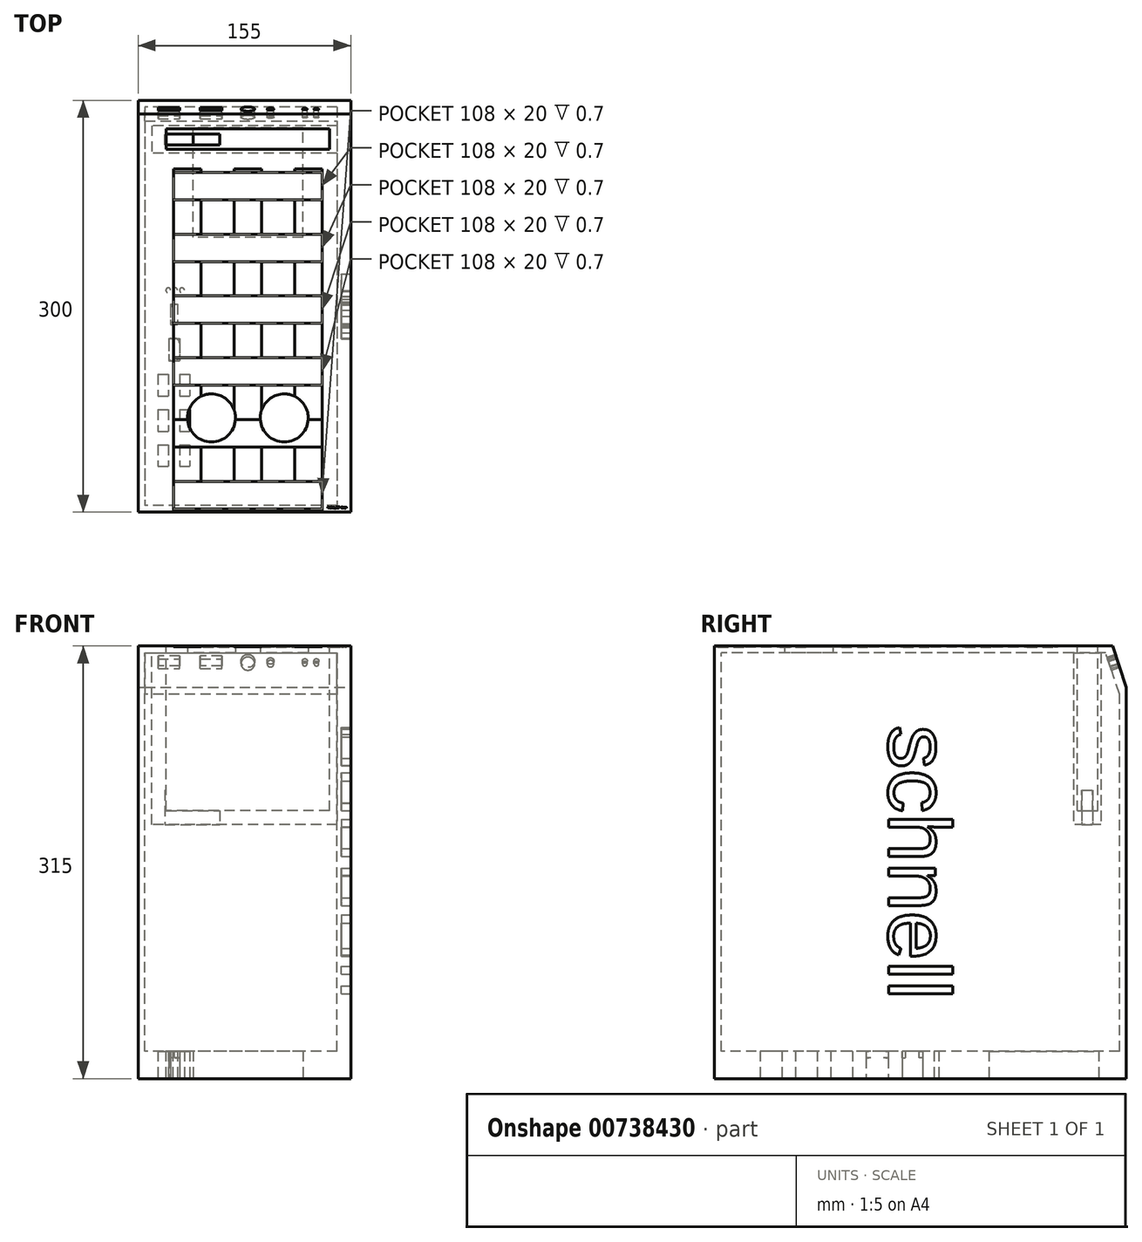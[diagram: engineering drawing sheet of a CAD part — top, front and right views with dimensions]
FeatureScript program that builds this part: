
annotation { "Feature Type Name" : "Feature", "Feature Type Description" : "" }
export const myFeature = defineFeature(function(context is Context, id is Id, definition is map)
    precondition{}
    {
        {
            var Q0;
            Q0=qCreatedBy(makeId("Top.planeOp"),FACE);
            var sketch = newSketch(context, id + "F0", { "sketchPlane" : qUnion([Q0])});
            skLineSegment(sketch, "E0.bottom", {"start": v(75, -150) * mm, "end": v(-75, -150) * mm});
            skLineSegment(sketch, "E0.top", {"start": v(75, 150) * mm, "end": v(-75, 150) * mm});
            skLineSegment(sketch, "E0.left", {"start": v(75, -150) * mm, "end": v(75, 150) * mm});
            skLineSegment(sketch, "E0.right", {"start": v(-75, -150) * mm, "end": v(-75, 150) * mm});
            skPoint(sketch, "E0.middle", {"position": v(0, 0) * mm});
            skSolve(sketch);
        }
        {
            var Q0;
            Q0 = qSketchRegion(id + "F0", true);
            extrude(context, id + "F1", {"entities" : qUnion([Q0]), "depth" : 300 * mm, "offsetDistance" : 25 * mm});
        }
        {
            var Q0;
            Q0=makeQuery(id+"F1.opExtrude","SWEPT_FACE",FACE,{"disambiguationData":[OSD([sQuery(id+"F0.wireOp",EDGE,"E0.left")])]});
            var sketch = newSketch(context, id + "F2", { "sketchPlane" : qUnion([Q0])});
            skLineSegment(sketch, "E1.bottom", {"start": v(145, 295) * mm, "end": v(-145, 295) * mm});
            skLineSegment(sketch, "E1.top", {"start": v(145, 5) * mm, "end": v(-145, 5) * mm});
            skLineSegment(sketch, "E1.left", {"start": v(145, 295) * mm, "end": v(145, 5) * mm});
            skLineSegment(sketch, "E1.right", {"start": v(-145, 295) * mm, "end": v(-145, 5) * mm});
            skPoint(sketch, "E1.middle", {"position": v(0, 150) * mm});
            skPoint(sketch, "E1.middle.positionSnap0", {"position": v(-150, 150) * mm});
            skPoint(sketch, "E1.centerSnap0", {"position": v(-150, 150) * mm});
            skSolve(sketch);
        }
        {
            var Q0;
            Q0 = qSketchRegion(id + "F2", true);
            extrude(context, id + "F3", {"entities" : qUnion([Q0]), "operationType" : NewBodyOperationType.REMOVE, "oppositeDirection" : true, "depth" : 140 * mm, "offsetDistance" : 25 * mm});
        }
        {
            var Q0;
            Q0=qCreatedBy(makeId("Top.planeOp"),FACE);
            var sketch = newSketch(context, id + "F4", { "sketchPlane" : qUnion([Q0])});
            skLineSegment(sketch, "E2.bottom", {"start": v(-70, 131.53) * mm, "end": v(70, 131.53) * mm});
            skLineSegment(sketch, "E2.top", {"start": v(-70, 111.53) * mm, "end": v(70, 111.53) * mm});
            skLineSegment(sketch, "E2.left", {"start": v(-70, 131.53) * mm, "end": v(-70, 111.53) * mm});
            skLineSegment(sketch, "E2.right", {"start": v(70, 131.53) * mm, "end": v(70, 111.53) * mm});
            skPoint(sketch, "E2.middle", {"position": v(0, 121.53) * mm});
            skSolve(sketch);
        }
        {
            var Q0;
            Q0 = qSketchRegion(id + "F4", true);
            extrude(context, id + "F5", {"entities" : qUnion([Q0]), "operationType" : NewBodyOperationType.ADD, "depth" : 130 * mm, "offsetDistance" : 25 * mm});
        }
        {
            var Q0;
            Q0=makeQuery(id+"F4.imprint","IMPRINT",FACE,{"disambiguationData":[TD([[makeQuery(id+"F4.imprint","IMPRINT",EDGE,{"derivedFrom":sQuery(id+"F4.wireOp",EDGE,"E2.bottom")}),-1.0]])]});
            var sketch = newSketch(context, id + "F6", { "sketchPlane" : qUnion([Q0])});
            skLineSegment(sketch, "E3.bottom", {"start": v(-59.38, 114.4) * mm, "end": v(59.38, 114.4) * mm});
            skLineSegment(sketch, "E3.top", {"start": v(-59.38, 129.2) * mm, "end": v(59.38, 129.2) * mm});
            skLineSegment(sketch, "E3.left", {"start": v(-59.38, 114.4) * mm, "end": v(-59.38, 129.2) * mm});
            skLineSegment(sketch, "E3.right", {"start": v(59.38, 114.4) * mm, "end": v(59.38, 129.2) * mm});
            skPoint(sketch, "E3.middle", {"position": v(0, 121.8) * mm});
            skSolve(sketch);
        }
        {
            var Q0;
            Q0 = qSketchRegion(id + "F6", true);
            extrude(context, id + "F7", {"entities" : qUnion([Q0]), "operationType" : NewBodyOperationType.REMOVE, "oppositeDirection" : true, "depth" : -120 * mm, "offsetDistance" : 25 * mm});
        }
        {
            var Q0;
            Q0=makeQuery(id+"F1.opExtrude","SWEPT_BODY",BODY,{"disambiguationData":[OSD([sQuery(id+"F0.wireOp",EDGE,"E0.bottom"),sQuery(id+"F0.wireOp",EDGE,"E0.top"),sQuery(id+"F0.wireOp",EDGE,"E0.left"),sQuery(id+"F0.wireOp",EDGE,"E0.right")])]});
            var Q1;
            Q1=sQuery(id+"F2.wireOp",EDGE,"E1.right");
            transform(context, id + "F8", {"entities" : qUnion([Q0]), "transformType" : TransformType.ROTATION, "transformAxis" : qUnion([Q1]), "angle" : 180 * degree, "makeCopy" : false});
        }
        {
            var Q0;
            Q0=makeQuery(id+"F1.opExtrude","SWEPT_BODY",BODY,{"disambiguationData":[OSD([sQuery(id+"F0.wireOp",EDGE,"E0.bottom"),sQuery(id+"F0.wireOp",EDGE,"E0.top"),sQuery(id+"F0.wireOp",EDGE,"E0.left"),sQuery(id+"F0.wireOp",EDGE,"E0.right")])]});
            var Q1;
            Q1=makeQuery(id+"F1.opExtrude","CAP_EDGE",EDGE,{"disambiguationData":[OSD([sQuery(id+"F0.wireOp",EDGE,"E0.bottom")])],"isStart":true});
            transform(context, id + "F9", {"entities" : qUnion([Q0]), "transformType" : TransformType.ROTATION, "transformAxis" : qUnion([Q1]), "angle" : 180 * degree, "makeCopy" : false});
        }
        {
            var Q0;
            Q0=makeQuery(id+"F1.opExtrude","CAP_EDGE",EDGE,{"disambiguationData":[OSD([sQuery(id+"F0.wireOp",EDGE,"E0.top")])],"isStart":true});
            var Q1;
            Q1=makeQuery(id+"F3.boolean.opBoolean","COPY",EDGE,{"derivedFrom":makeQuery(id+"F3.opExtrude","SWEPT_EDGE",EDGE,{"disambiguationData":[OSD([sQuery(id+"F2.wireOp",EDGE,"E1.top"),sQuery(id+"F2.wireOp",EDGE,"E1.left")])]})});
            chamfer(context, id + "F10", {"entities" : qUnion([Q0, Q1]), "chamferType" : ChamferType.TWO_OFFSETS, "width1" : 30 * mm, "oppositeDirection" : false, "width2" : 10 * mm, "tangentPropagation" : true});
        }
        {
            var Q0;
            Q0=makeQuery(id+"F10.opChamfer","BLEND_FACE",FACE,{"disambiguationData":[OSD([sQuery(id+"F0.wireOp",EDGE,"E0.top")])]});
            var sketch = newSketch(context, id + "F11", { "sketchPlane" : qUnion([Q0])});
            skLineSegment(sketch, "E4.bottom", {"start": v(-100.37, -55.09) * mm, "end": v(-84.67, -55.09) * mm});
            skLineSegment(sketch, "E4.top", {"start": v(-100.37, -62.59) * mm, "end": v(-84.67, -62.59) * mm});
            skLineSegment(sketch, "E4.left", {"start": v(-100.37, -55.09) * mm, "end": v(-100.37, -62.59) * mm});
            skLineSegment(sketch, "E4.right", {"start": v(-84.67, -55.09) * mm, "end": v(-84.67, -62.59) * mm});
            skPoint(sketch, "E4.middle", {"position": v(-92.52, -58.84) * mm});
            skLineSegment(sketch, "E5.bottom", {"start": v(-131.07, -55.09) * mm, "end": v(-115.37, -55.09) * mm});
            skLineSegment(sketch, "E5.top", {"start": v(-131.07, -62.59) * mm, "end": v(-115.37, -62.59) * mm});
            skLineSegment(sketch, "E5.left", {"start": v(-131.07, -55.09) * mm, "end": v(-131.07, -62.59) * mm});
            skLineSegment(sketch, "E5.right", {"start": v(-115.37, -55.09) * mm, "end": v(-115.37, -62.59) * mm});
            skPoint(sketch, "E5.middle", {"position": v(-123.22, -58.84) * mm});
            skPoint(sketch, "E5.cornerSnap0", {"position": v(-92.52, -55.09) * mm});
            skCircle(sketch, "E6", {"center": v(-191.47, -58.84) * mm, "radius": 1.75 * mm});
            skCircle(sketch, "E7", {"center": v(-199.97, -58.84) * mm, "radius": 1.75 * mm});
            skCircle(sketch, "E8", {"center": v(-150, -58.84) * mm, "radius": 5 * mm});
            skPoint(sketch, "E8.centerSnap0", {"position": v(-131.07, -58.84) * mm});
            skCircle(sketch, "E9", {"center": v(-166.5, -58.84) * mm, "radius": 2.5 * mm});
            skSolve(sketch);
        }
        {
            var Q0;
            Q0 = qSketchRegion(id + "F11", true);
            extrude(context, id + "F12", {"entities" : qUnion([Q0]), "operationType" : NewBodyOperationType.REMOVE, "oppositeDirection" : true, "depth" : 10 * mm, "offsetDistance" : 25 * mm});
        }
        {
            var Q0;
            Q0=makeQuery(id+"F11.imprint","IMPRINT",FACE,{"disambiguationData":[TD([[makeQuery(id+"F11.imprint","IMPRINT",EDGE,{"derivedFrom":sQuery(id+"F11.wireOp",EDGE,"E5.bottom")}),-1.0]])]});
            extrude(context, id + "F13", {"entities" : qUnion([Q0]), "operationType" : NewBodyOperationType.REMOVE, "oppositeDirection" : true, "depth" : 10 * mm, "offsetDistance" : 25 * mm});
        }
        {
            var Q0;
            Q0=makeQuery(id+"F1.opExtrude","CAP_FACE",FACE,{"disambiguationData":[OSD([sQuery(id+"F0.wireOp",EDGE,"E0.bottom"),sQuery(id+"F0.wireOp",EDGE,"E0.top"),sQuery(id+"F0.wireOp",EDGE,"E0.left"),sQuery(id+"F0.wireOp",EDGE,"E0.right")])],"isStart":false});
            var sketch = newSketch(context, id + "F14", { "sketchPlane" : qUnion([Q0])});
            skLineSegment(sketch, "E10.bottom", {"start": v(100.26, 91) * mm, "end": v(107.76, 91) * mm});
            skLineSegment(sketch, "E10.top", {"start": v(100.26, 106.7) * mm, "end": v(107.76, 106.7) * mm});
            skLineSegment(sketch, "E10.left", {"start": v(100.26, 91) * mm, "end": v(100.26, 106.7) * mm});
            skLineSegment(sketch, "E10.right", {"start": v(107.76, 91) * mm, "end": v(107.76, 106.7) * mm});
            skPoint(sketch, "E10.middle", {"position": v(104, 98.84) * mm});
            skLineSegment(sketch, "E11.bottom", {"start": v(84.56, 91) * mm, "end": v(92.06, 91) * mm});
            skLineSegment(sketch, "E11.top", {"start": v(84.56, 106.7) * mm, "end": v(92.06, 106.7) * mm});
            skLineSegment(sketch, "E11.left", {"start": v(84.56, 91) * mm, "end": v(84.56, 106.7) * mm});
            skLineSegment(sketch, "E11.right", {"start": v(92.06, 91) * mm, "end": v(92.06, 106.7) * mm});
            skPoint(sketch, "E11.middle", {"position": v(88.3, 98.84) * mm});
            skLineSegment(sketch, "E12.bottom", {"start": v(100.26, 65.3) * mm, "end": v(107.76, 65.3) * mm});
            skLineSegment(sketch, "E12.top", {"start": v(100.26, 81) * mm, "end": v(107.76, 81) * mm});
            skLineSegment(sketch, "E12.left", {"start": v(100.26, 65.3) * mm, "end": v(100.26, 81) * mm});
            skLineSegment(sketch, "E12.right", {"start": v(107.76, 65.3) * mm, "end": v(107.76, 81) * mm});
            skPoint(sketch, "E12.middle", {"position": v(104, 73.14) * mm});
            skLineSegment(sketch, "E13.bottom", {"start": v(84.56, 65.3) * mm, "end": v(92.06, 65.3) * mm});
            skLineSegment(sketch, "E13.top", {"start": v(84.56, 81) * mm, "end": v(92.06, 81) * mm});
            skLineSegment(sketch, "E13.left", {"start": v(84.56, 65.3) * mm, "end": v(84.56, 81) * mm});
            skLineSegment(sketch, "E13.right", {"start": v(92.06, 65.3) * mm, "end": v(92.06, 81) * mm});
            skPoint(sketch, "E13.middle", {"position": v(88.3, 73.14) * mm});
            skPoint(sketch, "E13.middle.positionSnap0", {"position": v(88.3, 91) * mm});
            skPoint(sketch, "E13.centerSnap0", {"position": v(88.3, 91) * mm});
            skLineSegment(sketch, "E14.bottom", {"start": v(100.26, 39.6) * mm, "end": v(107.76, 39.6) * mm});
            skLineSegment(sketch, "E14.top", {"start": v(100.26, 55.3) * mm, "end": v(107.76, 55.3) * mm});
            skLineSegment(sketch, "E14.left", {"start": v(100.26, 39.6) * mm, "end": v(100.26, 55.3) * mm});
            skLineSegment(sketch, "E14.right", {"start": v(107.76, 39.6) * mm, "end": v(107.76, 55.3) * mm});
            skPoint(sketch, "E14.middle", {"position": v(104, 47.44) * mm});
            skLineSegment(sketch, "E15.bottom", {"start": v(84.56, 39.6) * mm, "end": v(92.06, 39.6) * mm});
            skLineSegment(sketch, "E15.top", {"start": v(84.56, 55.3) * mm, "end": v(92.06, 55.3) * mm});
            skLineSegment(sketch, "E15.left", {"start": v(84.56, 39.6) * mm, "end": v(84.56, 55.3) * mm});
            skLineSegment(sketch, "E15.right", {"start": v(92.06, 39.6) * mm, "end": v(92.06, 55.3) * mm});
            skPoint(sketch, "E15.middle", {"position": v(88.3, 47.44) * mm});
            skSolve(sketch);
        }
        {
            var Q0;
            Q0 = qSketchRegion(id + "F14", true);
            extrude(context, id + "F15", {"entities" : qUnion([Q0]), "operationType" : NewBodyOperationType.REMOVE, "oppositeDirection" : true, "depth" : 10 * mm, "offsetDistance" : 25 * mm});
        }
        {
            var Q0;
            Q0=makeQuery(id+"F1.opExtrude","CAP_FACE",FACE,{"disambiguationData":[OSD([sQuery(id+"F0.wireOp",EDGE,"E0.bottom"),sQuery(id+"F0.wireOp",EDGE,"E0.top"),sQuery(id+"F0.wireOp",EDGE,"E0.left"),sQuery(id+"F0.wireOp",EDGE,"E0.right")])],"isStart":false});
            extrude(context, id + "F16", {"entities" : qUnion([Q0]), "operationType" : NewBodyOperationType.ADD, "depth" : 25 * mm, "offsetDistance" : 25 * mm});
        }
        {
            var Q0;
            Q0=makeQuery(id+"F16.opExtrude","CAP_FACE",FACE,{"disambiguationData":[OSD([sQuery(id+"F0.wireOp",EDGE,"E0.bottom"),sQuery(id+"F0.wireOp",EDGE,"E0.top"),sQuery(id+"F0.wireOp",EDGE,"E0.left"),sQuery(id+"F0.wireOp",EDGE,"E0.right")])],"isStart":false});
            var sketch = newSketch(context, id + "F17", { "sketchPlane" : qUnion([Q0])});
            skLineSegment(sketch, "E16.bottom", {"start": v(92.28, 13.4) * mm, "end": v(100.18, 13.4) * mm});
            skLineSegment(sketch, "E16.top", {"start": v(92.28, 29.6) * mm, "end": v(100.18, 29.6) * mm});
            skLineSegment(sketch, "E16.left", {"start": v(92.28, 13.4) * mm, "end": v(92.28, 29.6) * mm});
            skLineSegment(sketch, "E16.right", {"start": v(100.18, 13.4) * mm, "end": v(100.18, 29.6) * mm});
            skPoint(sketch, "E16.middle", {"position": v(96.23, 21.5) * mm});
            skLineSegment(sketch, "E17.bottom", {"start": v(93.73, -11.6) * mm, "end": v(98.73, -11.6) * mm});
            skLineSegment(sketch, "E17.top", {"start": v(93.73, 3.4) * mm, "end": v(98.73, 3.4) * mm});
            skLineSegment(sketch, "E17.left", {"start": v(93.73, -11.6) * mm, "end": v(93.73, 3.4) * mm});
            skLineSegment(sketch, "E17.right", {"start": v(98.73, -11.6) * mm, "end": v(98.73, 3.4) * mm});
            skPoint(sketch, "E17.middle", {"position": v(96.23, -4.1) * mm});
            skPoint(sketch, "E18.centerSnap0", {"position": v(104, 39.6) * mm});
            skCircle(sketch, "E19", {"center": v(102, -21.6) * mm, "radius": 1.75 * mm});
            skCircle(sketch, "E20", {"center": v(97, -21.6) * mm, "radius": 1.75 * mm});
            skCircle(sketch, "E21", {"center": v(92, -21.6) * mm, "radius": 1.75 * mm});
            skLineSegment(sketch, "E22.bottom", {"start": v(190, -60) * mm, "end": v(110, -60) * mm});
            skLineSegment(sketch, "E22.top", {"start": v(190, -140) * mm, "end": v(110, -140) * mm});
            skLineSegment(sketch, "E22.left", {"start": v(190, -60) * mm, "end": v(190, -140) * mm});
            skLineSegment(sketch, "E22.right", {"start": v(110, -60) * mm, "end": v(110, -140) * mm});
            skPoint(sketch, "E22.middle", {"position": v(150, -100) * mm});
            skSolve(sketch);
        }
        {
            var Q0;
            Q0=makeQuery(id+"F17.imprint","IMPRINT",FACE,{"disambiguationData":[TD([[makeQuery(id+"F17.imprint","IMPRINT",EDGE,{"derivedFrom":sQuery(id+"F17.wireOp",EDGE,"E16.bottom")}),-1.0]])]});
            extrude(context, id + "F18", {"entities" : qUnion([Q0]), "operationType" : NewBodyOperationType.REMOVE, "oppositeDirection" : true, "depth" : 10 * mm, "offsetDistance" : 25 * mm});
        }
        {
            var Q0;
            Q0 = qSketchRegion(id + "F17", true);
            extrude(context, id + "F19", {"entities" : qUnion([Q0]), "operationType" : NewBodyOperationType.REMOVE, "oppositeDirection" : true, "depth" : 50 * mm, "offsetDistance" : 25 * mm});
        }
        {
            var Q0;
            Q0=makeQuery(id+"F19.boolean.opBoolean","COPY",EDGE,{"derivedFrom":makeQuery(id+"F19.opExtrude","SWEPT_EDGE",EDGE,{"disambiguationData":[OSD([sQuery(id+"F17.wireOp",EDGE,"E16.bottom"),sQuery(id+"F17.wireOp",EDGE,"E16.right")])]})});
            var Q1;
            Q1=makeQuery(id+"F19.boolean.opBoolean","COPY",EDGE,{"derivedFrom":makeQuery(id+"F19.opExtrude","SWEPT_EDGE",EDGE,{"disambiguationData":[OSD([sQuery(id+"F17.wireOp",EDGE,"E16.top"),sQuery(id+"F17.wireOp",EDGE,"E16.right")])]})});
            fillet(context, id + "F20", {"entities" : qUnion([Q0, Q1]), "radius" : 3.5 * mm, "tangentPropagation" : true, "allowEdgeOverflow" : false});
        }
        {
            var Q0;
            Q0=makeQuery(id+"F19.boolean.opBoolean","COPY",EDGE,{"derivedFrom":makeQuery(id+"F19.opExtrude","SWEPT_EDGE",EDGE,{"disambiguationData":[OSD([sQuery(id+"F17.wireOp",EDGE,"E16.top"),sQuery(id+"F17.wireOp",EDGE,"E16.left")])]})});
            var Q1;
            Q1=makeQuery(id+"F19.boolean.opBoolean","COPY",EDGE,{"derivedFrom":makeQuery(id+"F19.opExtrude","SWEPT_EDGE",EDGE,{"disambiguationData":[OSD([sQuery(id+"F17.wireOp",EDGE,"E16.bottom"),sQuery(id+"F17.wireOp",EDGE,"E16.left")])]})});
            fillet(context, id + "F21", {"entities" : qUnion([Q0, Q1]), "radius" : 2 * mm, "tangentPropagation" : true, "allowEdgeOverflow" : false});
        }
        {
            var Q0;
            Q0=makeQuery(id+"F19.boolean.opBoolean","COPY",EDGE,{"derivedFrom":makeQuery(id+"F19.opExtrude","SWEPT_EDGE",EDGE,{"disambiguationData":[OSD([sQuery(id+"F17.wireOp",EDGE,"E17.bottom"),sQuery(id+"F17.wireOp",EDGE,"E17.left")])]})});
            var Q1;
            Q1=makeQuery(id+"F19.boolean.opBoolean","COPY",EDGE,{"derivedFrom":makeQuery(id+"F19.opExtrude","SWEPT_EDGE",EDGE,{"disambiguationData":[OSD([sQuery(id+"F17.wireOp",EDGE,"E17.top"),sQuery(id+"F17.wireOp",EDGE,"E17.left")])]})});
            chamfer(context, id + "F22", {"entities" : qUnion([Q0, Q1]), "width" : 2.5 * mm, "tangentPropagation" : true});
        }
        {
            var Q0;
            Q0=makeQuery(id+"F5.opExtrude","CAP_FACE",FACE,{"disambiguationData":[OSD([sQuery(id+"F4.wireOp",EDGE,"E2.bottom"),sQuery(id+"F4.wireOp",EDGE,"E2.top"),sQuery(id+"F4.wireOp",EDGE,"E2.left"),sQuery(id+"F4.wireOp",EDGE,"E2.right")])],"isStart":false});
            var sketch = newSketch(context, id + "F23", { "sketchPlane" : qUnion([Q0])});
            skLineSegment(sketch, "E23.bottom", {"start": v(89.4, -127.53) * mm, "end": v(129.4, -127.53) * mm});
            skLineSegment(sketch, "E23.top", {"start": v(89.4, -135.53) * mm, "end": v(129.4, -135.53) * mm});
            skLineSegment(sketch, "E23.left", {"start": v(89.4, -127.53) * mm, "end": v(89.4, -135.53) * mm});
            skLineSegment(sketch, "E23.right", {"start": v(129.4, -127.53) * mm, "end": v(129.4, -135.53) * mm});
            skPoint(sketch, "E23.middle", {"position": v(109.4, -131.53) * mm});
            skSolve(sketch);
        }
        {
            var Q0;
            Q0 = qSketchRegion(id + "F23", true);
            extrude(context, id + "F24", {"entities" : qUnion([Q0]), "operationType" : NewBodyOperationType.REMOVE, "oppositeDirection" : true, "depth" : 25 * mm, "offsetDistance" : 25 * mm});
        }
        {
            var Q0;
            Q0=makeQuery(id+"F1.opExtrude","CAP_FACE",FACE,{"disambiguationData":[OSD([sQuery(id+"F0.wireOp",EDGE,"E0.bottom"),sQuery(id+"F0.wireOp",EDGE,"E0.top"),sQuery(id+"F0.wireOp",EDGE,"E0.left"),sQuery(id+"F0.wireOp",EDGE,"E0.right")])],"isStart":true});
            var sketch = newSketch(context, id + "F25", { "sketchPlane" : qUnion([Q0])});
            skLineSegment(sketch, "E24.bottom", {"start": v(96, -140) * mm, "end": v(116, -140) * mm});
            skLineSegment(sketch, "E24.top", {"start": v(96, 110) * mm, "end": v(116, 110) * mm});
            skLineSegment(sketch, "E24.left", {"start": v(96, -140) * mm, "end": v(96, 110) * mm});
            skLineSegment(sketch, "E24.right", {"start": v(116, -140) * mm, "end": v(116, 110) * mm});
            skPoint(sketch, "E24.middle", {"position": v(106, -15) * mm});
            skLineSegment(sketch, "E25.bottom", {"start": v(160, -140) * mm, "end": v(140, -140) * mm});
            skLineSegment(sketch, "E25.top", {"start": v(160, 110) * mm, "end": v(140, 110) * mm});
            skLineSegment(sketch, "E25.left", {"start": v(160, -140) * mm, "end": v(160, 110) * mm});
            skLineSegment(sketch, "E25.right", {"start": v(140, -140) * mm, "end": v(140, 110) * mm});
            skPoint(sketch, "E25.middle", {"position": v(150, -15) * mm});
            skPoint(sketch, "E25.middle.positionSnap0", {"position": v(116, -15) * mm});
            skPoint(sketch, "E25.centerSnap0", {"position": v(116, -15) * mm});
            skLineSegment(sketch, "E26.bottom", {"start": v(204, -140) * mm, "end": v(184, -140) * mm});
            skLineSegment(sketch, "E26.top", {"start": v(204, 110) * mm, "end": v(184, 110) * mm});
            skLineSegment(sketch, "E26.left", {"start": v(204, -140) * mm, "end": v(204, 110) * mm});
            skLineSegment(sketch, "E26.right", {"start": v(184, -140) * mm, "end": v(184, 110) * mm});
            skPoint(sketch, "E26.middle", {"position": v(194, -15) * mm});
            skSolve(sketch);
        }
        {
            var Q0;
            Q0 = qSketchRegion(id + "F25", true);
            extrude(context, id + "F26", {"entities" : qUnion([Q0]), "operationType" : NewBodyOperationType.REMOVE, "oppositeDirection" : true, "depth" : 0.5 * mm, "offsetDistance" : 25 * mm});
        }
        {
            var Q0;
            Q0=makeQuery(id+"F1.opExtrude","CAP_FACE",FACE,{"disambiguationData":[OSD([sQuery(id+"F0.wireOp",EDGE,"E0.bottom"),sQuery(id+"F0.wireOp",EDGE,"E0.top"),sQuery(id+"F0.wireOp",EDGE,"E0.left"),sQuery(id+"F0.wireOp",EDGE,"E0.right")])],"isStart":true});
            var sketch = newSketch(context, id + "F27", { "sketchPlane" : qUnion([Q0])});
            skLineSegment(sketch, "E27.bottom", {"start": v(204, 87.5) * mm, "end": v(96, 87.5) * mm});
            skLineSegment(sketch, "E27.top", {"start": v(204, 107.5) * mm, "end": v(96, 107.5) * mm});
            skLineSegment(sketch, "E27.left", {"start": v(204, 87.5) * mm, "end": v(204, 107.5) * mm});
            skLineSegment(sketch, "E27.right", {"start": v(96, 87.5) * mm, "end": v(96, 107.5) * mm});
            skPoint(sketch, "E27.middle", {"position": v(150, 97.5) * mm});
            skPoint(sketch, "E27.middle.positionSnap0", {"position": v(150, 110) * mm});
            skPoint(sketch, "E27.centerSnap0", {"position": v(150, 110) * mm});
            skLineSegment(sketch, "E28.bottom", {"start": v(204, 42.5) * mm, "end": v(96, 42.5) * mm});
            skLineSegment(sketch, "E28.top", {"start": v(204, 62.5) * mm, "end": v(96, 62.5) * mm});
            skLineSegment(sketch, "E28.left", {"start": v(204, 42.5) * mm, "end": v(204, 62.5) * mm});
            skLineSegment(sketch, "E28.right", {"start": v(96, 42.5) * mm, "end": v(96, 62.5) * mm});
            skPoint(sketch, "E28.middle", {"position": v(150, 52.5) * mm});
            skLineSegment(sketch, "E29.bottom", {"start": v(204, -2.5) * mm, "end": v(96, -2.5) * mm});
            skLineSegment(sketch, "E29.top", {"start": v(204, 17.5) * mm, "end": v(96, 17.5) * mm});
            skLineSegment(sketch, "E29.left", {"start": v(204, -2.5) * mm, "end": v(204, 17.5) * mm});
            skLineSegment(sketch, "E29.right", {"start": v(96, -2.5) * mm, "end": v(96, 17.5) * mm});
            skPoint(sketch, "E29.middle", {"position": v(150, 7.5) * mm});
            skPoint(sketch, "E29.middle.positionSnap0", {"position": v(150, 42.5) * mm});
            skPoint(sketch, "E29.centerSnap0", {"position": v(150, 42.5) * mm});
            skLineSegment(sketch, "E30.bottom", {"start": v(204, -47.5) * mm, "end": v(96, -47.5) * mm});
            skLineSegment(sketch, "E30.top", {"start": v(204, -27.5) * mm, "end": v(96, -27.5) * mm});
            skLineSegment(sketch, "E30.left", {"start": v(204, -47.5) * mm, "end": v(204, -27.5) * mm});
            skLineSegment(sketch, "E30.right", {"start": v(96, -47.5) * mm, "end": v(96, -27.5) * mm});
            skPoint(sketch, "E30.middle", {"position": v(150, -37.5) * mm});
            skPoint(sketch, "E30.middle.positionSnap0", {"position": v(150, -2.5) * mm});
            skPoint(sketch, "E30.centerSnap0", {"position": v(150, -2.5) * mm});
            skLineSegment(sketch, "E31.bottom", {"start": v(204, -92.5) * mm, "end": v(96, -92.5) * mm});
            skLineSegment(sketch, "E31.top", {"start": v(204, -72.5) * mm, "end": v(96, -72.5) * mm});
            skLineSegment(sketch, "E31.left", {"start": v(204, -92.5) * mm, "end": v(204, -72.5) * mm});
            skLineSegment(sketch, "E31.right", {"start": v(96, -92.5) * mm, "end": v(96, -72.5) * mm});
            skPoint(sketch, "E31.middle", {"position": v(150, -82.5) * mm});
            skLineSegment(sketch, "E32.bottom", {"start": v(204, -117.5) * mm, "end": v(96, -117.5) * mm});
            skLineSegment(sketch, "E32.top", {"start": v(204, -137.5) * mm, "end": v(96, -137.5) * mm});
            skLineSegment(sketch, "E32.left", {"start": v(204, -117.5) * mm, "end": v(204, -137.5) * mm});
            skLineSegment(sketch, "E32.right", {"start": v(96, -117.5) * mm, "end": v(96, -137.5) * mm});
            skPoint(sketch, "E32.middle", {"position": v(150, -127.5) * mm});
            skText(sketch, "E33", { "text": "TheCrazyDEJV design", "fontName": "Arimo-Regular.ttf"});
            const initialGuessF27  = {"E33": [0.20795, -0.137, 1, 0, 0.001]};
            skSetInitialGuess(sketch, initialGuessF27);
            skSolve(sketch);
        }
        {
            var Q0;
            Q0 = qSketchRegion(id + "F27", true);
            extrude(context, id + "F28", {"entities" : qUnion([Q0]), "operationType" : NewBodyOperationType.REMOVE, "oppositeDirection" : true, "depth" : 0.7 * mm, "offsetDistance" : 25 * mm});
        }
        {
            var Q0;
            Q0 = qSketchRegion(id + "F27", true);
            extrude(context, id + "F29", {"entities" : qUnion([Q0]), "operationType" : NewBodyOperationType.REMOVE, "oppositeDirection" : true, "depth" : 0.7 * mm, "offsetDistance" : 25 * mm});
        }
        {
            var Q0;
            {var subQ0=sQuery(id+"F0.wireOp",EDGE,"E0.right");Q0=makeQuery(id+"F16.boolean.opBoolean","MERGE",FACE,{"derivedFrom":[makeQuery(id+"F1.opExtrude","SWEPT_FACE",FACE,{"disambiguationData":[OSD([subQ0])]}),makeQuery(id+"F16.opExtrude","SWEPT_FACE",FACE,{"disambiguationData":[OSD([subQ0])]})]});}
            var sketch = newSketch(context, id + "F30", { "sketchPlane" : qUnion([Q0])});
            skText(sketch, "E34", { "text": "schnell", "fontName": "Arimo-Regular.ttf"});
            const initialGuessF30  = {"E34": [-0.01311, -0.0575, 0, -1, 0.04623]};
            skSetInitialGuess(sketch, initialGuessF30);
            skSolve(sketch);
        }
        {
            var Q0;
            Q0 = qSketchRegion(id + "F30", true);
            extrude(context, id + "F31", {"entities" : qUnion([Q0]), "operationType" : NewBodyOperationType.REMOVE, "oppositeDirection" : true, "depth" : 7 * mm, "offsetDistance" : 25 * mm});
        }
        {
            var Q0;
            Q0 = qSketchRegion(id + "F17", true);
            extrude(context, id + "F32", {"entities" : qUnion([Q0]), "operationType" : NewBodyOperationType.REMOVE, "oppositeDirection" : true, "depth" : 25 * mm, "offsetDistance" : 25 * mm});
        }
        {
            var Q0;
            Q0=makeQuery(id+"F3.boolean.opBoolean","COPY",FACE,{"derivedFrom":makeQuery(id+"F3.opExtrude","SWEPT_FACE",FACE,{"disambiguationData":[OSD([sQuery(id+"F2.wireOp",EDGE,"E1.top")])]})});
            var sketch = newSketch(context, id + "F33", { "sketchPlane" : qUnion([Q0])});
            skCircle(sketch, "E35", {"center": v(123.5, 71.36) * mm, "radius": 17.5 * mm});
            skCircle(sketch, "E36", {"center": v(176.5, 71.36) * mm, "radius": 17.5 * mm});
            skSolve(sketch);
        }
        {
            var Q0;
            Q0 = qSketchRegion(id + "F33", true);
            extrude(context, id + "F34", {"entities" : qUnion([Q0]), "operationType" : NewBodyOperationType.REMOVE, "oppositeDirection" : true, "depth" : 25 * mm, "offsetDistance" : 25 * mm});
        }
        {
            var Q0;
            {var subQ0=sQuery(id+"F0.wireOp",EDGE,"E0.left");Q0=makeQuery(id+"F16.boolean.opBoolean","MERGE",FACE,{"derivedFrom":[makeQuery(id+"F1.opExtrude","SWEPT_FACE",FACE,{"disambiguationData":[OSD([subQ0])]}),makeQuery(id+"F16.opExtrude","SWEPT_FACE",FACE,{"disambiguationData":[OSD([subQ0])]})]});}
            cPlane(context, id + "F35", {"entities" : qUnion([Q0]), "cplaneType" : CPlaneType.OFFSET, "offset" : 0 * mm, "width" : 150 * mm, "height" : 150 * mm});
        }
        {
            var Q0;
            Q0=qCreatedBy(id+"F35.planeOp",FACE);
            var sketch = newSketch(context, id + "F36", { "sketchPlane" : qUnion([Q0])});
            skLineSegment(sketch, "E37.bottom", {"start": v(-160, -315) * mm, "end": v(140, -315) * mm});
            skLineSegment(sketch, "E37.top", {"start": v(-160, 0) * mm, "end": v(140, 0) * mm});
            skLineSegment(sketch, "E37.left", {"start": v(-160, -315) * mm, "end": v(-160, 0) * mm});
            skLineSegment(sketch, "E37.right", {"start": v(140, -315) * mm, "end": v(140, 0) * mm});
            skSolve(sketch);
        }
        {
            var Q0;
            Q0 = qSketchRegion(id + "F36", true);
            extrude(context, id + "F37", {"entities" : qUnion([Q0]), "operationType" : NewBodyOperationType.ADD, "depth" : 5 * mm, "offsetDistance" : 25 * mm});
        }
        {
            var Q0;
            Q0=makeQuery(id+"F37.opExtrude","SWEPT_EDGE",EDGE,{"disambiguationData":[OSD([sQuery(id+"F36.wireOp",EDGE,"E37.top"),sQuery(id+"F36.wireOp",EDGE,"E37.left")])]});
            chamfer(context, id + "F38", {"entities" : qUnion([Q0]), "chamferType" : ChamferType.TWO_OFFSETS, "width1" : 30 * mm, "oppositeDirection" : false, "width2" : 10 * mm, "tangentPropagation" : true});
        }
    });
